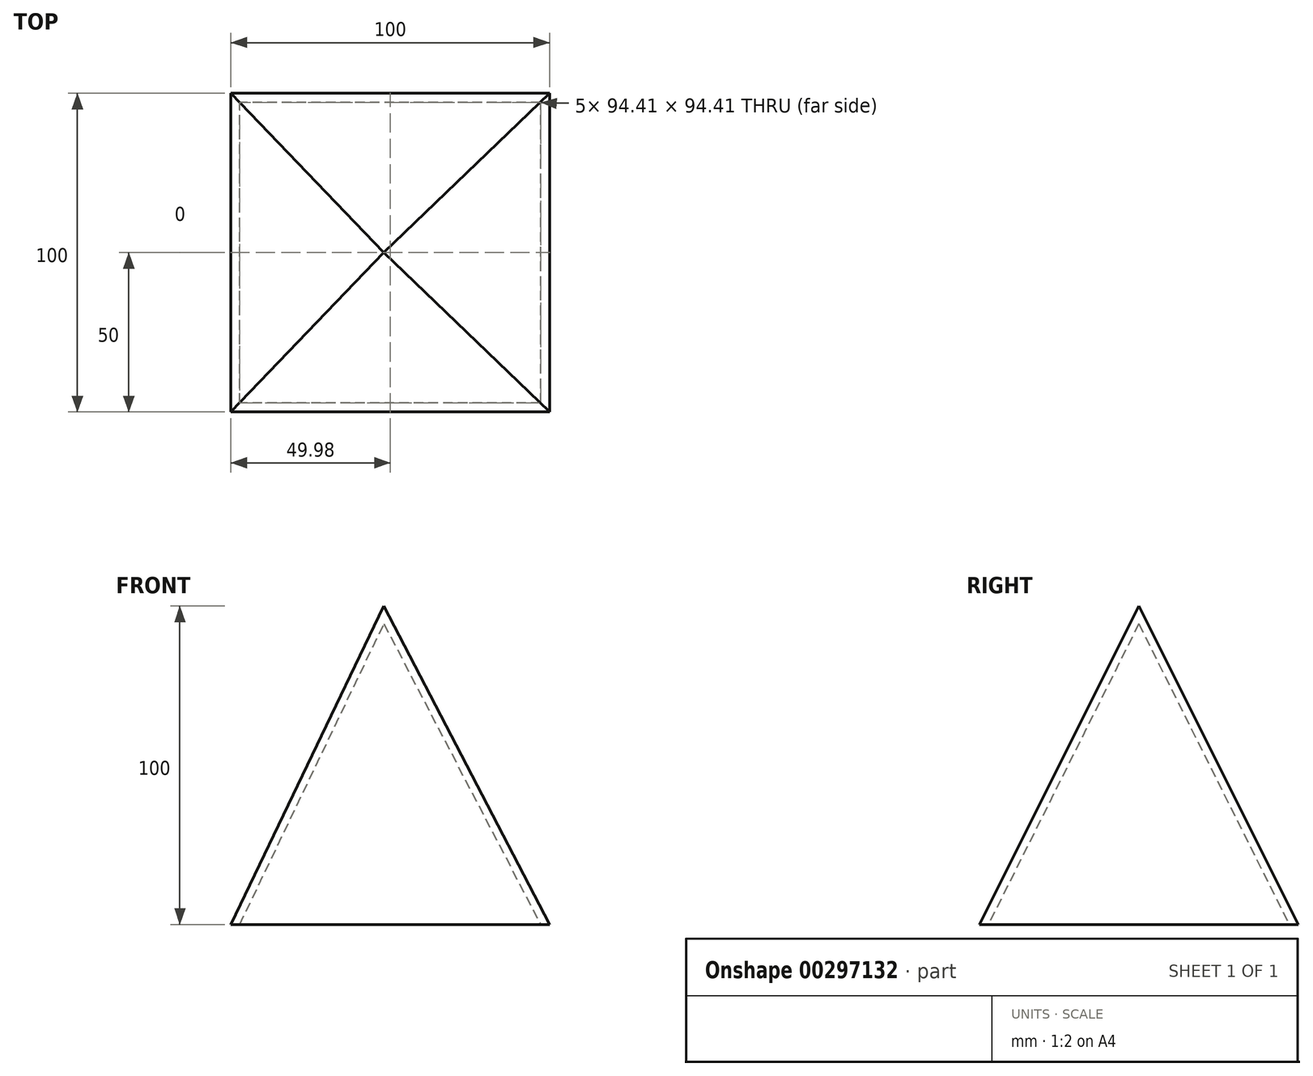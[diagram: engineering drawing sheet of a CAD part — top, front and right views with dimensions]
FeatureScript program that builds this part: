
annotation { "Feature Type Name" : "Feature", "Feature Type Description" : "" }
export const myFeature = defineFeature(function(context is Context, id is Id, definition is map)
    precondition{}
    {
        {
            var Q0;
            Q0=qCreatedBy(makeId("Top.planeOp"),FACE);
            var sketch = newSketch(context, id + "F0", { "sketchPlane" : qUnion([Q0])});
            skLineSegment(sketch, "E0.bottom", {"start": v(52.1, -50) * mm, "end": v(-47.9, -50) * mm});
            skLineSegment(sketch, "E0.top", {"start": v(52.1, 50) * mm, "end": v(-47.9, 50) * mm});
            skLineSegment(sketch, "E0.left", {"start": v(52.1, -50) * mm, "end": v(52.1, 50) * mm});
            skLineSegment(sketch, "E0.right", {"start": v(-47.9, -50) * mm, "end": v(-47.9, 50) * mm});
            skPoint(sketch, "E0.middle", {"position": v(2.1, 0) * mm});
            skSolve(sketch);
        }
        {
            var Q0;
            Q0=qCreatedBy(makeId("Top.planeOp"),FACE);
            cPlane(context, id + "F1", {"entities" : qUnion([Q0]), "cplaneType" : CPlaneType.OFFSET, "offset" : 100 * mm, "width" : 150 * mm, "height" : 150 * mm});
        }
        {
            var Q0;
            Q0=qCreatedBy(id+"F1.planeOp",FACE);
            var sketch = newSketch(context, id + "F2", { "sketchPlane" : qUnion([Q0])});
            skPoint(sketch, "E1", {"position": v(0, 0) * mm});
            skSolve(sketch);
        }
        {
            var Q0;
            Q0=makeQuery(id+"F0.imprint","IMPRINT",FACE,{"disambiguationData":[TD([[makeQuery(id+"F0.imprint","IMPRINT",EDGE,{"derivedFrom":sQuery(id+"F0.wireOp",EDGE,"E0.bottom")}),-1.0]])]});
            var Q1;
            Q1=sQuery(id+"F2.wireOp",VERTEX,"E1");
            loft(context, id + "F3", {"sheetProfilesArray" : [{ "sheetProfileEntities" : qUnion([Q0]) }, { "sheetProfileEntities" : qUnion([Q1]) }]});
        }
        {
            var Q0;
            Q0=makeQuery(id+"F3.opLoft","CAP_FACE",FACE,{"disambiguationData":[OSD([makeQuery(id+"F0.imprint","IMPRINT",FACE,{"disambiguationData":[TD([[makeQuery(id+"F0.imprint","IMPRINT",EDGE,{"derivedFrom":sQuery(id+"F0.wireOp",EDGE,"E0.bottom")}),-1.0]])]})])],"isStart":true});
            shell(context, id + "F4", {"entities" : qUnion([Q0]), "thickness" : 2.5 * mm});
        }
    });
